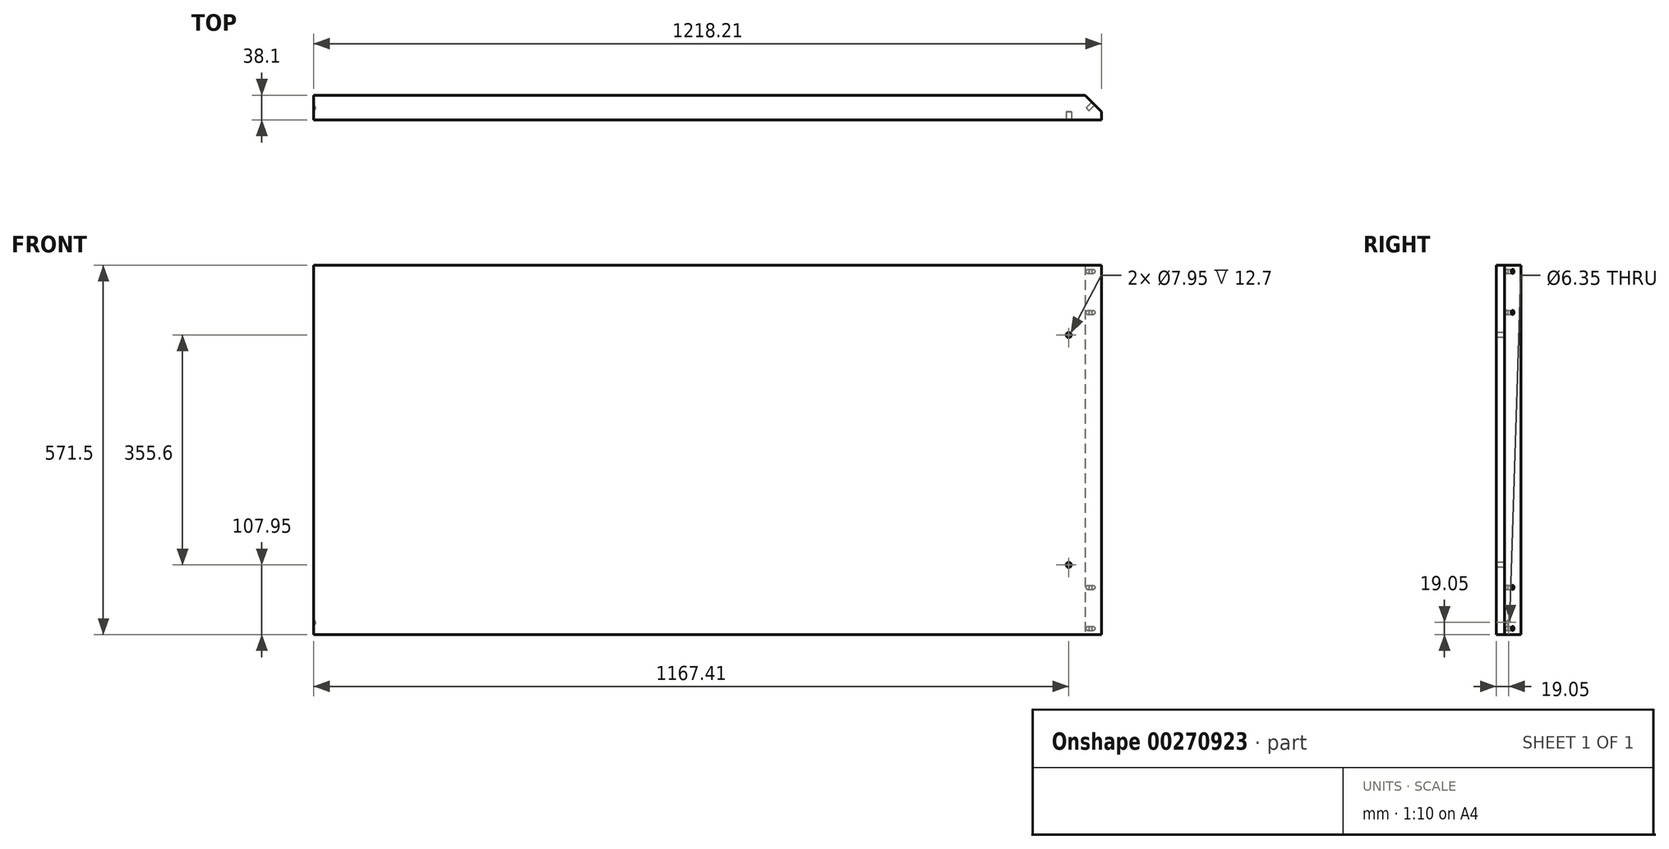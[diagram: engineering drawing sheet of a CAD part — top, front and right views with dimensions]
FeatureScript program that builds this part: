
annotation { "Feature Type Name" : "Feature", "Feature Type Description" : "" }
export const myFeature = defineFeature(function(context is Context, id is Id, definition is map)
    precondition{}
    {
        {
            var Q0;
            Q0=qCreatedBy(makeId("Front.planeOp"),FACE);
            var sketch = newSketch(context, id + "F0", { "sketchPlane" : qUnion([Q0])});
            skLineSegment(sketch, "E0.top", {"start": v(0, -571.5) * mm, "end": v(1218.2, -571.5) * mm});
            skLineSegment(sketch, "E0.left", {"start": v(0, -6.35) * mm, "end": v(0, -571.5) * mm});
            skLineSegment(sketch, "E0.right", {"start": v(1218.2, -6.35) * mm, "end": v(1218.2, -571.5) * mm});
            skPoint(sketch, "E1.orphan", {"position": v(0, 0) * mm});
            skLineSegment(sketch, "E2", {"start": v(0, -6.35) * mm, "end": v(0, 0) * mm});
            skLineSegment(sketch, "E3", {"start": v(1218.2, -6.35) * mm, "end": v(1218.2, 0) * mm});
            skLineSegment(sketch, "E4", {"start": v(1218.2, 0) * mm, "end": v(0, 0) * mm});
            skSolve(sketch);
        }
        {
            var Q0;
            Q0=qSketchRegion(id+"F0",true);
            extrude(context, id + "F1", {"entities" : qUnion([Q0]), "depth" : 38.1 * mm});
        }
        {
            var Q0;
            Q0=makeQuery(id+"F1.opExtrude","SWEPT_FACE",FACE,{"disambiguationData":[OSD([sQuery(id+"F0.wireOp",EDGE,"E0.left")])]});
            var sketch = newSketch(context, id + "F2", { "sketchPlane" : qUnion([Q0])});
            skLineSegment(sketch, "E5.bottom", {"start": v(0, -571.5) * mm, "end": v(38.1, -571.5) * mm});
            skLineSegment(sketch, "E5.top", {"start": v(0, -609.6) * mm, "end": v(38.1, -609.6) * mm});
            skLineSegment(sketch, "E5.left", {"start": v(0, -571.5) * mm, "end": v(0, -609.6) * mm});
            skLineSegment(sketch, "E5.right", {"start": v(38.1, -571.5) * mm, "end": v(38.1, -609.6) * mm});
            skLineSegment(sketch, "E6", {"start": v(19.05, -609.6) * mm, "end": v(19.05, -590.55) * mm});
            skPoint(sketch, "E6.endSnap0", {"position": v(0, -590.55) * mm});
            skLineSegment(sketch, "E7.top", {"start": v(0, -533.4) * mm, "end": v(38.1, -533.4) * mm});
            skLineSegment(sketch, "E7.left", {"start": v(0, -571.5) * mm, "end": v(0, -533.4) * mm});
            skLineSegment(sketch, "E7.right", {"start": v(38.1, -571.5) * mm, "end": v(38.1, -533.4) * mm});
            skLineSegment(sketch, "E8", {"start": v(19.05, -571.5) * mm, "end": v(19.05, -552.45) * mm});
            skPoint(sketch, "E8.endSnap0", {"position": v(0, -552.45) * mm});
            skLineSegment(sketch, "E9.MirrorCS", {"start": v(0, -495.3) * mm, "end": v(38.1, -495.3) * mm});
            skLineSegment(sketch, "E10.MirrorCS", {"start": v(0, -495.3) * mm, "end": v(0, -533.4) * mm});
            skLineSegment(sketch, "E11.MirrorCS", {"start": v(38.1, -495.3) * mm, "end": v(38.1, -533.4) * mm});
            skLineSegment(sketch, "E12.MirrorCS", {"start": v(19.05, -495.3) * mm, "end": v(19.05, -514.35) * mm});
            skLineSegment(sketch, "E13", {"start": v(0, -285.75) * mm, "end": v(38.1, -285.75) * mm});
            skLineSegment(sketch, "E14.MirrorCS", {"start": v(0, -38.1) * mm, "end": v(38.1, -38.1) * mm});
            skLineSegment(sketch, "E15.MirrorCS", {"start": v(38.1, 0) * mm, "end": v(38.1, -38.1) * mm});
            skLineSegment(sketch, "E16.MirrorCS", {"start": v(0, 0) * mm, "end": v(0, -38.1) * mm});
            skLineSegment(sketch, "E17.MirrorCS", {"start": v(0, 0) * mm, "end": v(38.1, 0) * mm});
            skLineSegment(sketch, "E18.MirrorCS", {"start": v(19.05, 0) * mm, "end": v(19.05, -19.05) * mm});
            skSolve(sketch);
        }
        {
            var Q0;
            Q0=sQuery(id+"F2.wireOp",VERTEX,"E8.end");
            var Q1;
            Q1=sQuery(id+"F2.wireOp",VERTEX,"E6.end");
            var Q2;
            Q2=makeQuery(id+"F1.opExtrude","SWEPT_BODY",BODY,{"disambiguationData":[OSD([sQuery(id+"F0.wireOp",EDGE,"E0.top"),sQuery(id+"F0.wireOp",EDGE,"E0.left"),sQuery(id+"F0.wireOp",EDGE,"E0.right"),sQuery(id+"F0.wireOp",EDGE,"gDhKNAhB-mvM7-LPII-0QTI-d5j6MYJOtABQ")])]});
            hole(context, id + "F3", {"style" : HoleStyle.SIMPLE, "endStyle" : HoleEndStyle.BLIND, "holeDiameter" : 6.35 * mm, "holeDepth" : 1.52 * mm, "tappedDepth" : 12.7 * mm, "tapClearance" : 3, "locations" : qUnion([Q0, Q1]), "scope" : qUnion([Q2])});
        }
        {
            var Q0;
            Q0=makeQuery(id+"F1.opExtrude","CAP_EDGE",EDGE,{"disambiguationData":[OSD([sQuery(id+"F0.wireOp",EDGE,"E0.right"),sQuery(id+"F0.wireOp",EDGE,"E3")])],"isStart":true});
            chamfer(context, id + "F4", {"entities" : qUnion([Q0]), "chamferType" : ChamferType.OFFSET_ANGLE, "width" : 25.4 * mm, "oppositeDirection" : false, "angle" : 45 * degree, "tangentPropagation" : true});
        }
        {
            var Q0;
            Q0=makeQuery(id+"F4.opChamfer","BLEND_FACE",FACE,{"disambiguationData":[OSD([sQuery(id+"F0.wireOp",EDGE,"E0.right"),sQuery(id+"F0.wireOp",EDGE,"E3")])]});
            var sketch = newSketch(context, id + "F5", { "sketchPlane" : qUnion([Q0])});
            skLineSegment(sketch, "E19", {"start": v(-861.4, -571.5) * mm, "end": v(-861.4, 0) * mm});
            skLineSegment(sketch, "E20", {"start": v(-879.36, -285.75) * mm, "end": v(-843.44, -285.75) * mm});
            skLineSegment(sketch, "E21", {"start": v(-879.36, -571.5) * mm, "end": v(-879.36, -561.98) * mm});
            skLineSegment(sketch, "E22", {"start": v(-879.36, -561.98) * mm, "end": v(-861.4, -561.98) * mm});
            skLineSegment(sketch, "E23", {"start": v(-861.4, -561.98) * mm, "end": v(-861.4, -498.47) * mm});
            skCircle(sketch, "E24", {"center": v(-861.4, -561.98) * mm, "radius": 3.18 * mm});
            skCircle(sketch, "E25", {"center": v(-861.4, -498.47) * mm, "radius": 3.18 * mm});
            skCircle(sketch, "E26.MirrorC", {"center": v(-861.4, -73.02) * mm, "radius": 3.18 * mm});
            skCircle(sketch, "E27.MirrorC", {"center": v(-861.4, -9.52) * mm, "radius": 3.18 * mm});
            skSolve(sketch);
        }
        {
            var Q0;
            Q0=qSketchRegion(id+"F5",true);
            extrude(context, id + "F6", {"entities" : qUnion([Q0]), "operationType" : NewBodyOperationType.REMOVE, "oppositeDirection" : true, "depth" : 12.7 * mm});
        }
        {
            var Q0;
            Q0=makeQuery(id+"F1.opExtrude","CAP_FACE",FACE,{"disambiguationData":[OSD([sQuery(id+"F0.wireOp",EDGE,"E0.top"),sQuery(id+"F0.wireOp",EDGE,"E0.left"),sQuery(id+"F0.wireOp",EDGE,"E0.right"),sQuery(id+"F0.wireOp",EDGE,"E2"),sQuery(id+"F0.wireOp",EDGE,"E3"),sQuery(id+"F0.wireOp",EDGE,"E4")])],"isStart":false});
            var sketch = newSketch(context, id + "F7", { "sketchPlane" : qUnion([Q0])});
            skLineSegment(sketch, "E28", {"start": v(1218.2, 0) * mm, "end": v(1167.4, 0) * mm});
            skLineSegment(sketch, "E29", {"start": v(1167.4, 0) * mm, "end": v(1167.4, -107.95) * mm});
            skCircle(sketch, "E30", {"center": v(1167.4, -107.95) * mm, "radius": 3.98 * mm});
            skLineSegment(sketch, "E31", {"start": v(1218.2, -285.75) * mm, "end": v(1008.9, -285.75) * mm});
            skCircle(sketch, "E32.MirrorC", {"center": v(1167.4, -463.55) * mm, "radius": 3.98 * mm});
            skLineSegment(sketch, "E33", {"start": v(1218.2, 0) * mm, "end": v(1218.2, -38.1) * mm});
            skSolve(sketch);
        }
        {
            var Q0;
            Q0=qSketchRegion(id+"F7",true);
            extrude(context, id + "F8", {"entities" : qUnion([Q0]), "operationType" : NewBodyOperationType.REMOVE, "oppositeDirection" : true, "depth" : 12.7 * mm});
        }
    });
